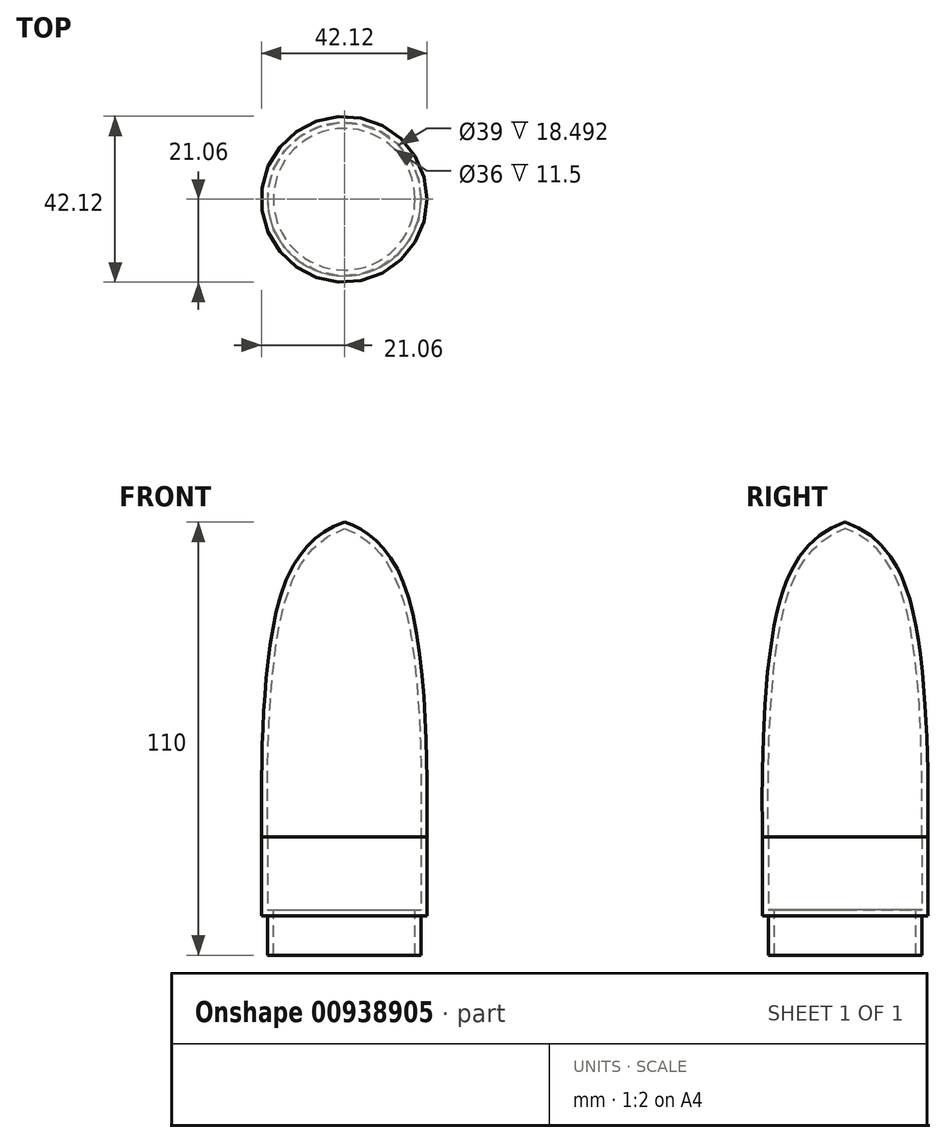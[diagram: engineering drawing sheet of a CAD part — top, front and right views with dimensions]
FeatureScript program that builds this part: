
annotation { "Feature Type Name" : "Feature", "Feature Type Description" : "" }
export const myFeature = defineFeature(function(context is Context, id is Id, definition is map)
    precondition{}
    {
        {
            var Q0;
            Q0=qCreatedBy(makeId("Front.planeOp"),FACE);
            var sketch = newSketch(context, id + "F0", { "sketchPlane" : qUnion([Q0])});
            skLineSegment(sketch, "E0", {"start": v(0, 0) * mm, "end": v(0, 100) * mm});
            skLineSegment(sketch, "E1", {"start": v(0, 0) * mm, "end": v(21, 0) * mm});
            skLineSegment(sketch, "E2", {"start": v(21, 0) * mm, "end": v(21, 20) * mm});
            skFitSpline(sketch, "E3", {"points": [v(0, 100) * mm, v(16.26, 81.05) * mm, v(21, 20) * mm], "startDerivative": vector(46.45, -15.12) * mm, "endDerivative": vector(0.23, -20.1) * mm});
            skLineSegment(sketch, "E4", {"start": v(0, 0) * mm, "end": v(0, 127.8) * mm, "construction": true});
            skSolve(sketch);
        }
        {
            var Q0;
            Q0=qSketchRegion(id+"F0",true);
            var Q1;
            Q1=sQuery(id+"F0.wireOp",EDGE,"E4");
            revolve(context, id + "F1", {"surfaceOperationType" : NewSurfaceOperationType.NEW, "entities" : qUnion([Q0]), "axis" : qUnion([Q1]), "revolveType" : RevolveType.FULL});
        }
        {
            var Q0;
            Q0=makeQuery(id+"F1.opRevolve","SWEPT_FACE",FACE,{"disambiguationData":[OSD([sQuery(id+"F0.wireOp",EDGE,"E1")])]});
            var sketch = newSketch(context, id + "F2", { "sketchPlane" : qUnion([Q0])});
            skCircle(sketch, "E5", {"center": v(0, 0) * mm, "radius": 19.5 * mm});
            skSolve(sketch);
        }
        {
            var Q0;
            Q0=qSketchRegion(id+"F2",true);
            extrude(context, id + "F3", {"entities" : qUnion([Q0]), "operationType" : NewBodyOperationType.ADD, "depth" : 10 * mm, "offsetDistance" : 25 * mm});
        }
        {
            var Q0;
            Q0=makeQuery(id+"F3.opExtrude","CAP_FACE",FACE,{"disambiguationData":[OSD([sQuery(id+"F2.wireOp",EDGE,"E5")])],"isStart":false});
            shell(context, id + "F4", {"entities" : qUnion([Q0]), "thickness" : 1.5 * mm});
        }
    });
